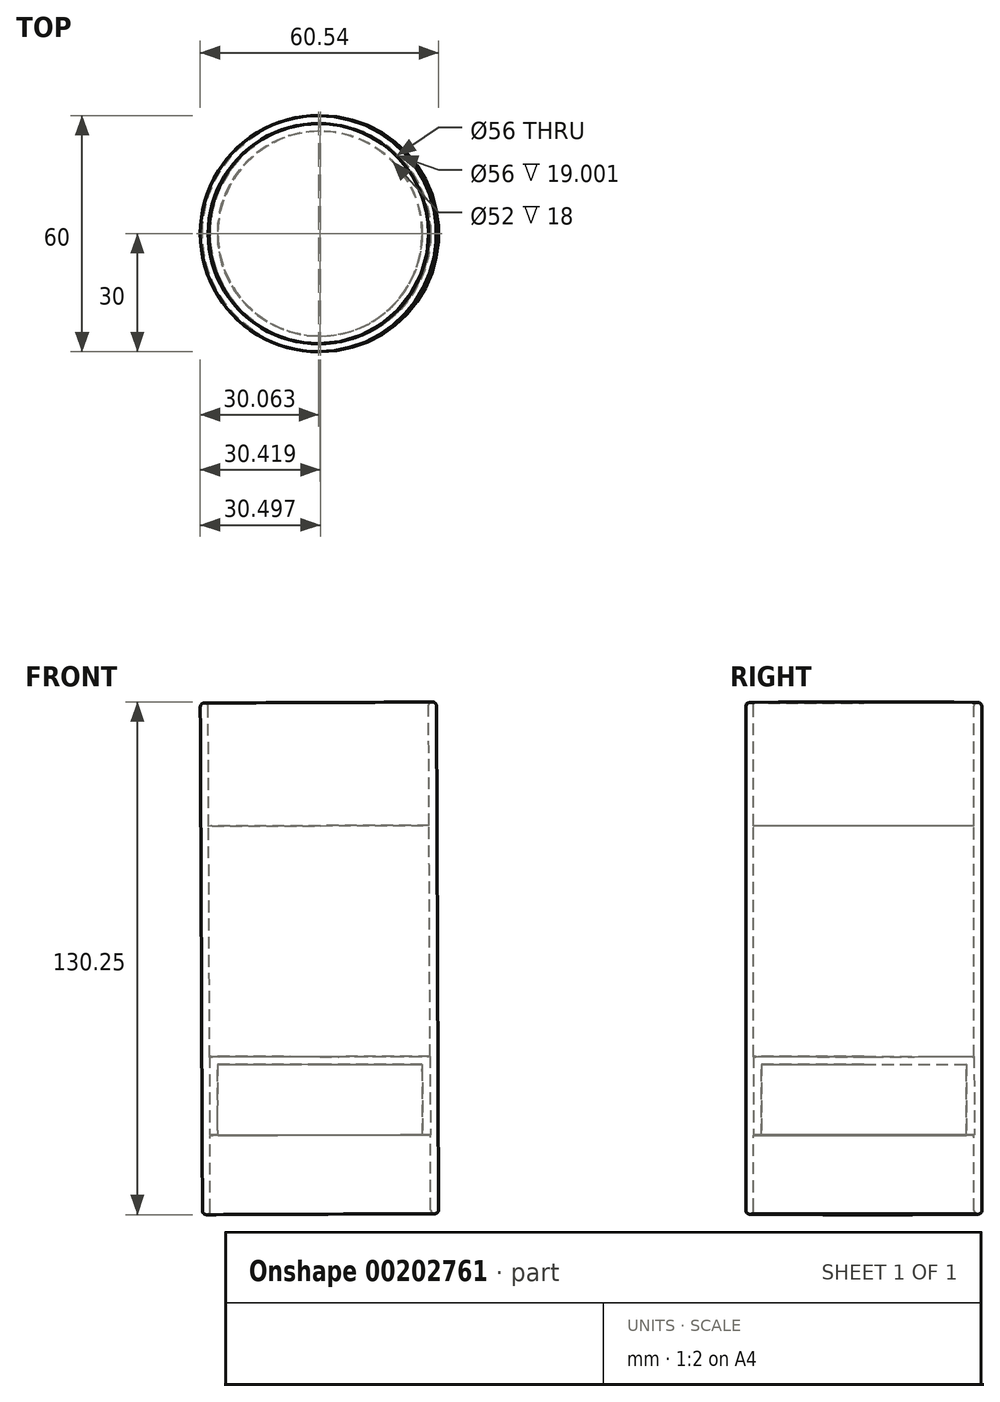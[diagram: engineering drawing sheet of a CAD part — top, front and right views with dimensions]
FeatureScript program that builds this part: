
annotation { "Feature Type Name" : "Feature", "Feature Type Description" : "" }
export const myFeature = defineFeature(function(context is Context, id is Id, definition is map)
    precondition{}
    {
        {
            var Q0;
            Q0=qCreatedBy(makeId("Front.planeOp"),FACE);
            var sketch = newSketch(context, id + "F0", { "sketchPlane" : qUnion([Q0])});
            skLineSegment(sketch, "E0", {"start": v(-14.5, 23.97) * mm, "end": v(-16.5, 23.97) * mm});
            skLineSegment(sketch, "E1", {"start": v(-16.5, 23.97) * mm, "end": v(-15.96, -106.03) * mm});
            skLineSegment(sketch, "E2", {"start": v(-15.96, -106.03) * mm, "end": v(-13.96, -106.03) * mm});
            skLineSegment(sketch, "E3", {"start": v(-13.96, -106.03) * mm, "end": v(-14.04, -86.03) * mm});
            skLineSegment(sketch, "E4", {"start": v(-14.5, 23.97) * mm, "end": v(-14.37, -7.34) * mm});
            skSolve(sketch);
        }
        {
            var Q0;
            Q0=qCreatedBy(makeId("Front.planeOp"),FACE);
            var sketch = newSketch(context, id + "F1", { "sketchPlane" : qUnion([Q0])});
            skLineSegment(sketch, "E5", {"start": v(-14.04, -86.03) * mm, "end": v(-14.13, -66.03) * mm});
            skLineSegment(sketch, "E6", {"start": v(-14.13, -66.03) * mm, "end": v(13.87, -65.9) * mm});
            skLineSegment(sketch, "E7.0", {"start": v(-12.12, -68.02) * mm, "end": v(13.88, -67.9) * mm});
            skLineSegment(sketch, "E7.1", {"start": v(-12.04, -86.02) * mm, "end": v(-12.12, -68.02) * mm});
            skLineSegment(sketch, "E8", {"start": v(-12.04, -86.02) * mm, "end": v(-14.04, -86.03) * mm});
            skPoint(sketch, "E9.0.start.orphan", {"position": v(-13.96, -106.03) * mm});
            skLineSegment(sketch, "E10", {"start": v(13.88, -69.6) * mm, "end": v(13.87, -24.21) * mm, "construction": true});
            skSolve(sketch);
        }
        {
            var Q0;
            Q0=qCreatedBy(makeId("Front.planeOp"),FACE);
            var sketch = newSketch(context, id + "F2", { "sketchPlane" : qUnion([Q0])});
            skLineSegment(sketch, "E11.0", {"start": v(-14.13, -66.03) * mm, "end": v(13.87, -65.9) * mm});
            skLineSegment(sketch, "E12", {"start": v(-14.37, -7.34) * mm, "end": v(-14.13, -66.03) * mm});
            skPoint(sketch, "E13.0.start.orphan", {"position": v(-14.5, 23.97) * mm});
            skLineSegment(sketch, "E14", {"start": v(13.87, -65.9) * mm, "end": v(13.49, 26.25) * mm, "construction": true});
            skSolve(sketch);
        }
        {
            var Q0;
            Q0=sQuery(id+"F0.wireOp",EDGE,"E1");
            var Q1;
            Q1=sQuery(id+"F0.wireOp",EDGE,"E4");
            var Q2;
            Q2=sQuery(id+"F0.wireOp",EDGE,"E0");
            var Q3;
            Q3=sQuery(id+"F0.wireOp",EDGE,"E2");
            var Q4;
            Q4=sQuery(id+"F0.wireOp",EDGE,"E3");
            var Q5;
            Q5=sQuery(id+"F1.wireOp",EDGE,"E8");
            var Q6;
            Q6=sQuery(id+"F1.wireOp",EDGE,"E7.1");
            var Q7;
            Q7=sQuery(id+"F1.wireOp",EDGE,"E7.0");
            var Q8;
            Q8=sQuery(id+"F2.wireOp",EDGE,"E14");
            revolve(context, id + "F3", {"bodyType" : ToolBodyType.SURFACE, "surfaceEntities" : qUnion([Q0, Q1, Q2, Q3, Q4, Q5, Q6, Q7]), "axis" : qUnion([Q8]), "revolveType" : RevolveType.FULL});
        }
        {
            var Q0;
            Q0=sQuery(id+"F2.wireOp",EDGE,"E12");
            var Q1;
            Q1=sQuery(id+"F2.wireOp",EDGE,"E11.0");
            var Q2;
            Q2=sQuery(id+"F2.wireOp",EDGE,"E14");
            revolve(context, id + "F4", {"bodyType" : ToolBodyType.SURFACE, "surfaceEntities" : qUnion([Q0, Q1]), "axis" : qUnion([Q2]), "revolveType" : RevolveType.FULL});
        }
        {
            var Q0;
            Q0=qCreatedBy(makeId("Front.planeOp"),FACE);
            var sketch = newSketch(context, id + "F5", { "sketchPlane" : qUnion([Q0])});
            skLineSegment(sketch, "E15.0", {"start": v(13.63, -7.22) * mm, "end": v(-14.37, -7.34) * mm});
            skLineSegment(sketch, "E16", {"start": v(13.63, -7.22) * mm, "end": v(13.59, 1.57) * mm, "construction": true});
            skPoint(sketch, "E17.orphan", {"position": v(41.63, -7.1) * mm});
            skSolve(sketch);
        }
        {
            var Q0;
            Q0 = qSketchRegion(id + "F5", true);
            var Q1;
            Q1=sQuery(id+"F5.wireOp",EDGE,"E15.0");
            var Q2;
            Q2=sQuery(id+"F5.wireOp",EDGE,"E16");
            revolve(context, id + "F6", {"bodyType" : ToolBodyType.SURFACE, "entities" : qUnion([Q0]), "surfaceEntities" : qUnion([Q1]), "axis" : qUnion([Q2]), "revolveType" : RevolveType.FULL});
        }
        {
            var Q0;
            Q0=makeQuery(id+"F3.opRevolve","SWEPT_FACE",FACE,{"disambiguationData":[OSD([sQuery(id+"F0.wireOp",EDGE,"E0")])]});
            var Q1;
            Q1=makeQuery(id+"F3.opRevolve","SWEPT_FACE",FACE,{"disambiguationData":[OSD([sQuery(id+"F0.wireOp",EDGE,"E2")])]});
            fillet(context, id + "F7", {"entities" : qUnion([Q0, Q1]), "radius" : 1 * mm, "tangentPropagation" : true, "allowEdgeOverflow" : false});
        }
        {
            var Q0;
            Q0=qCreatedBy(makeId("Front.planeOp"),FACE);
            var sketch = newSketch(context, id + "F8", { "sketchPlane" : qUnion([Q0])});
            skLineSegment(sketch, "E18.0", {"start": v(39.96, -85.8) * mm, "end": v(41.96, -85.8) * mm});
            skLineSegment(sketch, "E19.0", {"start": v(13.87, -65.9) * mm, "end": v(41.87, -65.8) * mm});
            skLineSegment(sketch, "E20.0", {"start": v(13.87, -67.9) * mm, "end": v(39.88, -67.8) * mm});
            skLineSegment(sketch, "E21", {"start": v(39.88, -67.8) * mm, "end": v(39.96, -85.8) * mm});
            skLineSegment(sketch, "E22", {"start": v(41.87, -65.8) * mm, "end": v(41.96, -85.8) * mm});
            skLineSegment(sketch, "E23", {"start": v(13.87, -65.9) * mm, "end": v(13.87, -67.9) * mm});
            skPoint(sketch, "E24.orphan", {"position": v(-14.13, -66.03) * mm});
            skPoint(sketch, "E25.orphan", {"position": v(-12.12, -68.02) * mm});
            skPoint(sketch, "E26.orphan", {"position": v(-14.04, -86.03) * mm});
            skSolve(sketch);
        }
        {
            var Q0;
            Q0 = qSketchRegion(id + "F8", true);
            var Q1;
            Q1=sQuery(id+"F8.wireOp",EDGE,"E19.0");
            var Q2;
            Q2=sQuery(id+"F8.wireOp",EDGE,"E22");
            var Q3;
            Q3=sQuery(id+"F8.wireOp",EDGE,"E21");
            var Q4;
            Q4=sQuery(id+"F8.wireOp",EDGE,"E18.0");
            var Q5;
            Q5=sQuery(id+"F8.wireOp",EDGE,"E20.0");
            var Q6;
            Q6=sQuery(id+"F8.wireOp",EDGE,"E23");
            revolve(context, id + "F9", {"bodyType" : ToolBodyType.SURFACE, "entities" : qUnion([Q0]), "surfaceEntities" : qUnion([Q1, Q2, Q3, Q4, Q5]), "axis" : qUnion([Q6]), "revolveType" : RevolveType.FULL});
        }
    });
